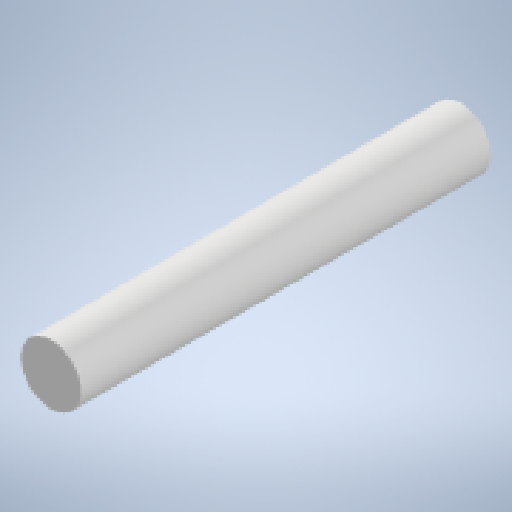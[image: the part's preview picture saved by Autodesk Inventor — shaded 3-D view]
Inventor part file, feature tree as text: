
AUTODESK INVENTOR PART (.ipt)
format: ipt  version: 2024.3 (Build 283343000, 343)  size: 133,120 bytes
history: native  units: mm
features: other x2, extrude x1, sketch x1, reference x1
ambient origin geometry x8: Origin, YZ Plane, XZ Plane, XY Plane, X Axis, Y Axis, Z Axis, Center Point
bodies: Solid1 (feature_tree)
feature tree (5):
  extrude  "Extrusion1"  [1 undecoded]
  sketch  "Sketch1"  dims[d0=26.0mm d1=0.0mm]
  reference  "Reference1"
  other  "Assembly1"
  other  "housing:1"
note: 1 required parameter value undecoded (feature->parameter linkage not recoverable at this tier; creation-order binding heuristic only, values carry confidence <= 0.55)
